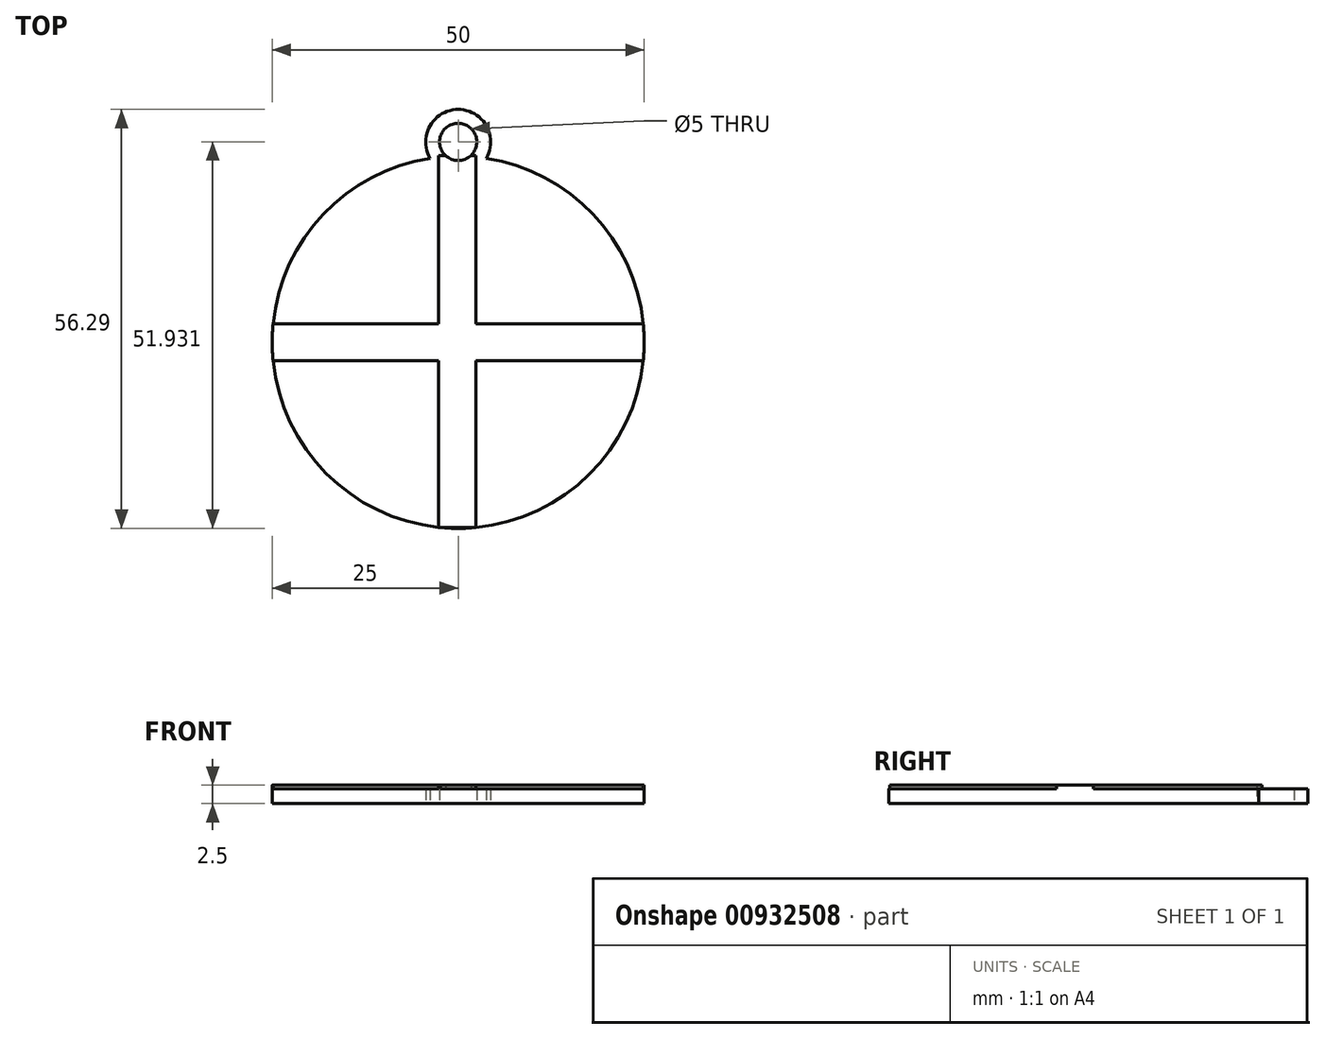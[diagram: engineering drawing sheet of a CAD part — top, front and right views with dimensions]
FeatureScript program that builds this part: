
annotation { "Feature Type Name" : "Feature", "Feature Type Description" : "" }
export const myFeature = defineFeature(function(context is Context, id is Id, definition is map)
    precondition{}
    {
        {
            var Q0;
            Q0=qCreatedBy(makeId("Top.planeOp"),FACE);
            var sketch = newSketch(context, id + "F0", { "sketchPlane" : qUnion([Q0])});
            skCircle(sketch, "E0", {"center": v(0, 0) * mm, "radius": 25 * mm});
            skCircle(sketch, "E1", {"center": v(0, 26.93) * mm, "radius": 4.36 * mm});
            skSolve(sketch);
        }
        {
            var Q0;
            {var subQ0=sQuery(id+"F0.wireOp",EDGE,"E1");var subQ1=sQuery(id+"F0.wireOp",EDGE,"E0");var subQ2=makeQuery(id+"F0.imprint","INTERSECT",VERTEX,{"disambiguationData":[OD(0.0)],"derivedFrom":[subQ1,subQ0]});Q0=makeQuery(id+"F0.imprint","IMPRINT",FACE,{"disambiguationData":[TD([[makeQuery(id+"F0.imprint","IMPRINT",EDGE,{"disambiguationData":[TD([[subQ2,1.0]])],"derivedFrom":subQ1}),-1.0]])]});}
            var Q1;
            {var subQ0=sQuery(id+"F0.wireOp",EDGE,"E1");var subQ1=sQuery(id+"F0.wireOp",EDGE,"E0");var subQ2=makeQuery(id+"F0.imprint","INTERSECT",VERTEX,{"disambiguationData":[OD(0.0)],"derivedFrom":[subQ1,subQ0]});Q1=makeQuery(id+"F0.imprint","IMPRINT",FACE,{"disambiguationData":[TD([[makeQuery(id+"F0.imprint","IMPRINT",EDGE,{"disambiguationData":[TD([[subQ2,1.0]])],"derivedFrom":subQ1}),1.0]])]});}
            var Q2;
            {var subQ0=sQuery(id+"F0.wireOp",EDGE,"E1");var subQ1=sQuery(id+"F0.wireOp",EDGE,"E0");var subQ2=makeQuery(id+"F0.imprint","INTERSECT",VERTEX,{"disambiguationData":[OD(0.0)],"derivedFrom":[subQ1,subQ0]});Q2=makeQuery(id+"F0.imprint","IMPRINT",FACE,{"disambiguationData":[TD([[makeQuery(id+"F0.imprint","IMPRINT",EDGE,{"disambiguationData":[TD([[subQ2,-1.0]])],"derivedFrom":subQ1}),1.0]])]});}
            var Q3;
            Q3 = qSketchRegion(id + "F2", true);
            extrude(context, id + "F1", {"entities" : qUnion([Q0, Q1, Q2, Q3]), "depth" : 2 * mm, "offsetDistance" : 25 * mm});
        }
        {
            var Q0;
            Q0=makeQuery(id+"F1.opExtrude","CAP_FACE",FACE,{"disambiguationData":[OSD([sQuery(id+"F0.wireOp",EDGE,"E0"),sQuery(id+"F0.wireOp",EDGE,"E1")])],"isStart":false});
            var sketch = newSketch(context, id + "F2", { "sketchPlane" : qUnion([Q0])});
            skLineSegment(sketch, "E2.top", {"start": v(-25, 2.5) * mm, "end": v(25, 2.5) * mm});
            skLineSegment(sketch, "E2.left", {"start": v(-25, 0) * mm, "end": v(-25, 2.5) * mm});
            skLineSegment(sketch, "E2.right", {"start": v(25, 0) * mm, "end": v(25, 2.5) * mm});
            skLineSegment(sketch, "E3.MirrorCS", {"start": v(25, 0) * mm, "end": v(25, -2.5) * mm});
            skLineSegment(sketch, "E4.MirrorCS", {"start": v(-25, -2.5) * mm, "end": v(25, -2.5) * mm});
            skLineSegment(sketch, "E5.MirrorCS", {"start": v(-25, 0) * mm, "end": v(-25, -2.5) * mm});
            skLineSegment(sketch, "E6.top", {"start": v(-2.64, -24.89) * mm, "end": v(-2.64, 25.11) * mm});
            skLineSegment(sketch, "E6.left", {"start": v(-0.14, -24.89) * mm, "end": v(-2.64, -24.89) * mm});
            skLineSegment(sketch, "E6.right", {"start": v(-0.14, 25.11) * mm, "end": v(-2.64, 25.11) * mm});
            skLineSegment(sketch, "E7.MirrorCS", {"start": v(-0.14, 25.11) * mm, "end": v(2.36, 25.11) * mm});
            skLineSegment(sketch, "E8.MirrorCS", {"start": v(2.36, -24.89) * mm, "end": v(2.36, 25.11) * mm});
            skLineSegment(sketch, "E9.MirrorCS", {"start": v(-0.14, -24.89) * mm, "end": v(2.36, -24.89) * mm});
            skSolve(sketch);
        }
        {
            var Q0;
            {var subQ1=sQuery(id+"F2.wireOp",EDGE,"E6.right");Q0=makeQuery(id+"F2.imprint","IMPRINT",FACE,{"disambiguationData":[TD([[makeQuery(id+"F2.imprint","IMPRINT",EDGE,{"derivedFrom":subQ1}),1.0]])]});}
            var Q1;
            {var subQ2=sQuery(id+"F2.wireOp",EDGE,"E2.top");var subQ4=sQuery(id+"F2.wireOp",EDGE,"E6.top");var subQ8=makeQuery(id+"F2.imprint","INTERSECT",VERTEX,{"derivedFrom":[subQ2,subQ4]});Q1=makeQuery(id+"F2.imprint","IMPRINT",FACE,{"disambiguationData":[TD([[makeQuery(id+"F2.imprint","IMPRINT",EDGE,{"disambiguationData":[TD([[subQ8,1.0]])],"derivedFrom":subQ2}),-1.0]])]});}
            var Q2;
            {var subQ0=sQuery(id+"F2.wireOp",EDGE,"E6.top");var subQ1=sQuery(id+"F2.wireOp",EDGE,"E2.top");var subQ2=makeQuery(id+"F2.imprint","INTERSECT",VERTEX,{"derivedFrom":[subQ1,subQ0]});Q2=makeQuery(id+"F2.imprint","IMPRINT",FACE,{"disambiguationData":[TD([[makeQuery(id+"F2.imprint","IMPRINT",EDGE,{"disambiguationData":[TD([[subQ2,-1.0]])],"derivedFrom":subQ1}),-1.0]])]});}
            var Q3;
            {var subQ2=sQuery(id+"F2.wireOp",EDGE,"E2.top");var subQ4=sQuery(id+"F2.wireOp",EDGE,"E8.MirrorCS");var subQ8=makeQuery(id+"F2.imprint","INTERSECT",VERTEX,{"derivedFrom":[subQ2,subQ4]});Q3=makeQuery(id+"F2.imprint","IMPRINT",FACE,{"disambiguationData":[TD([[makeQuery(id+"F2.imprint","IMPRINT",EDGE,{"disambiguationData":[TD([[subQ8,-1.0]])],"derivedFrom":subQ2}),-1.0]])]});}
            var Q4;
            {var subQ0=sQuery(id+"F2.wireOp",EDGE,"E9.MirrorCS");Q4=makeQuery(id+"F2.imprint","IMPRINT",FACE,{"disambiguationData":[TD([[makeQuery(id+"F2.imprint","IMPRINT",EDGE,{"derivedFrom":subQ0}),1.0]])]});}
            extrude(context, id + "F3", {"entities" : qUnion([Q0, Q1, Q2, Q3, Q4]), "operationType" : NewBodyOperationType.ADD, "depth" : 0.5 * mm, "offsetDistance" : 25 * mm});
        }
        {
            var Q0;
            Q0=sQuery(id+"F0.wireOp",VERTEX,"E1.center");
            var Q1;
            Q1=makeQuery(id+"F1.opExtrude","SWEPT_BODY",BODY,{"disambiguationData":[OSD([sQuery(id+"F0.wireOp",EDGE,"E0"),sQuery(id+"F0.wireOp",EDGE,"E1")])]});
            var Q2;
            Q2=makeQuery(id+"FxbFwKo7378SfdE_1.opExtrude","SWEPT_BODY",BODY,{"disambiguationData":[OSD([sQuery(id+"F2.wireOp",EDGE,"E2.top"),sQuery(id+"F2.wireOp",EDGE,"E6.top"),sQuery(id+"F2.wireOp",EDGE,"E6.right"),sQuery(id+"F2.wireOp",EDGE,"E7.MirrorCS"),sQuery(id+"F2.wireOp",EDGE,"E8.MirrorCS")])]});
            hole(context, id + "F4", {"style" : HoleStyle.SIMPLE, "endStyle" : HoleEndStyle.THROUGH, "oppositeDirection" : true, "holeDiameter" : 5 * mm, "majorDiameter" : 5 * mm, "isTappedThrough" : true, "tappedDepth" : 12 * mm, "tapClearance" : 3, "locations" : qUnion([Q0]), "scope" : qUnion([Q1, Q2])});
        }
    });
